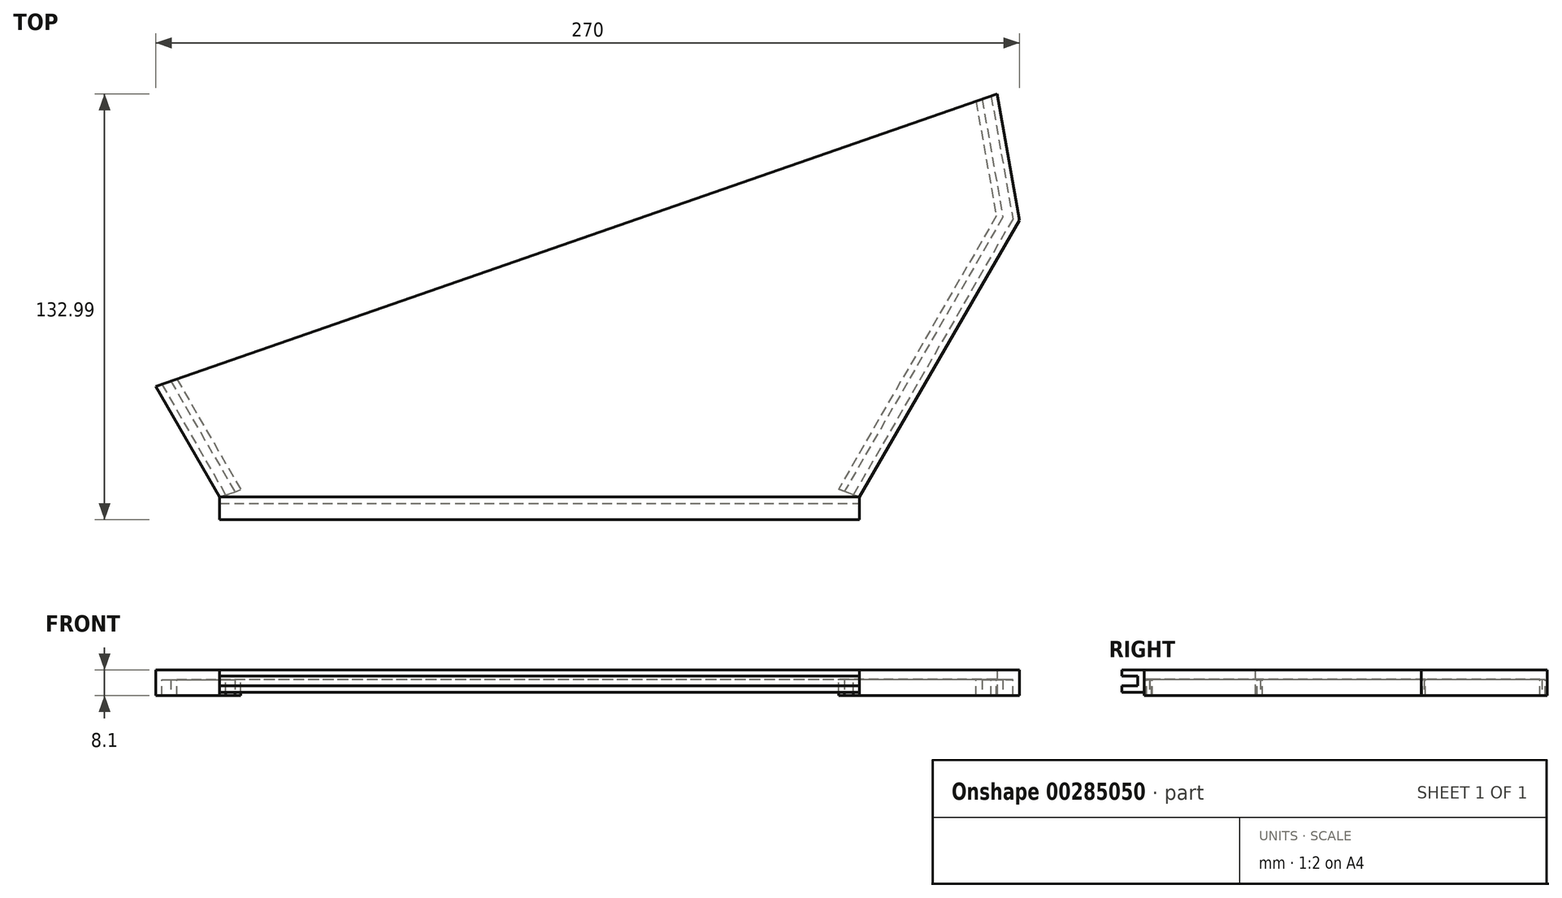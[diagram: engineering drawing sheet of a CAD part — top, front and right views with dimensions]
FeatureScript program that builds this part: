
annotation { "Feature Type Name" : "Feature", "Feature Type Description" : "" }
export const myFeature = defineFeature(function(context is Context, id is Id, definition is map)
    precondition{}
    {
        {
            var Q0;
            Q0=qCreatedBy(makeId("Top.planeOp"),FACE);
            var sketch = newSketch(context, id + "F0", { "sketchPlane" : qUnion([Q0])});
            skLineSegment(sketch, "E0", {"start": v(-20, 34.64) * mm, "end": v(0, 0) * mm});
            skLineSegment(sketch, "E1", {"start": v(0, 0) * mm, "end": v(200, 0) * mm});
            skLineSegment(sketch, "E2", {"start": v(200, 0) * mm, "end": v(250, 86.6) * mm});
            skLineSegment(sketch, "E3", {"start": v(250, 86.6) * mm, "end": v(243.05, 126) * mm});
            skLineSegment(sketch, "E4", {"start": v(-20, 34.64) * mm, "end": v(243.05, 126) * mm});
            skSolve(sketch);
        }
        {
            var Q0;
            Q0=makeQuery(id+"F0.imprint","IMPRINT",FACE,{"disambiguationData":[TD([[makeQuery(id+"F0.imprint","IMPRINT",EDGE,{"derivedFrom":sQuery(id+"F0.wireOp",EDGE,"E0")}),1.0]])]});
            extrude(context, id + "F1", {"entities" : qUnion([Q0]), "depth" : 3 * mm});
        }
        {
            var Q0;
            Q0=makeQuery(id+"F1.opExtrude","SWEPT_FACE",FACE,{"disambiguationData":[OSD([sQuery(id+"F0.wireOp",EDGE,"E4")])]});
            var sketch = newSketch(context, id + "F2", { "sketchPlane" : qUnion([Q0])});
            skLineSegment(sketch, "E5", {"start": v(7.53, 0) * mm, "end": v(7.53, -5.1) * mm});
            skLineSegment(sketch, "E6", {"start": v(7.53, -5.1) * mm, "end": v(5.53, -5.1) * mm});
            skLineSegment(sketch, "E7", {"start": v(5.53, -5.1) * mm, "end": v(5.53, -0.1) * mm});
            skLineSegment(sketch, "E8", {"start": v(5.53, -0.1) * mm, "end": v(2.53, -0.1) * mm});
            skLineSegment(sketch, "E9", {"start": v(2.53, -0.1) * mm, "end": v(2.53, -5.1) * mm});
            skLineSegment(sketch, "E10", {"start": v(2.53, -5.1) * mm, "end": v(0.53, -5.1) * mm});
            skLineSegment(sketch, "E11", {"start": v(0.53, -5.1) * mm, "end": v(0.53, 0) * mm});
            skSolve(sketch);
        }
        {
            var Q0;
            {var subQ0=sQuery(id+"F0.wireOp",EDGE,"E4");Q0=makeQuery(id+"F4.boolean.opBoolean","MERGE",FACE,{"derivedFrom":[makeQuery(id+"F1.opExtrude","SWEPT_FACE",FACE,{"disambiguationData":[OSD([subQ0])]}),makeQuery(id+"F4.opSweep","CAP_FACE",FACE,{"disambiguationData":[OSD([sQuery(id+"F0.wireOp",EDGE,"E0"),subQ0,sQuery(id+"F2.wireOp",EDGE,"E5"),sQuery(id+"F2.wireOp",EDGE,"E6"),sQuery(id+"F2.wireOp",EDGE,"E7"),sQuery(id+"F2.wireOp",EDGE,"E8"),sQuery(id+"F2.wireOp",EDGE,"E9"),sQuery(id+"F2.wireOp",EDGE,"E10"),sQuery(id+"F2.wireOp",EDGE,"E11")])],"isStart":true})]});}
            var sketch = newSketch(context, id + "F3", { "sketchPlane" : qUnion([Q0])});
            skLineSegment(sketch, "E12", {"start": v(-270.94, 0) * mm, "end": v(-270.94, -5.1) * mm});
            skLineSegment(sketch, "E13", {"start": v(-270.94, -5.1) * mm, "end": v(-268.94, -5.1) * mm});
            skLineSegment(sketch, "E14", {"start": v(-268.94, -5.1) * mm, "end": v(-268.94, -0.1) * mm});
            skLineSegment(sketch, "E15", {"start": v(-268.94, -0.1) * mm, "end": v(-265.94, -0.1) * mm});
            skLineSegment(sketch, "E16", {"start": v(-265.94, -0.1) * mm, "end": v(-265.94, -5.1) * mm});
            skLineSegment(sketch, "E17", {"start": v(-265.94, -5.1) * mm, "end": v(-263.94, -5.1) * mm});
            skLineSegment(sketch, "E18", {"start": v(-263.94, -5.1) * mm, "end": v(-263.94, 0) * mm});
            skLineSegment(sketch, "E19", {"start": v(-263.94, 0) * mm, "end": v(-270.94, 0) * mm});
            skSolve(sketch);
        }
        {
            var Q0;
            {var subQ0=sQuery(id+"F2.wireOp",EDGE,"E5");Q0=makeQuery(id+"F2.imprint","IMPRINT",FACE,{"disambiguationData":[TD([[makeQuery(id+"F2.imprint","IMPRINT",EDGE,{"derivedFrom":subQ0}),-1.0]])]});}
            var Q1;
            Q1=makeQuery(id+"F1.opExtrude","CAP_EDGE",EDGE,{"disambiguationData":[OSD([sQuery(id+"F0.wireOp",EDGE,"E0")])],"isStart":true});
            sweep(context, id + "F4", {"operationType" : NewBodyOperationType.ADD, "profiles" : qUnion([Q0]), "path" : qUnion([Q1])});
        }
        {
            var Q0;
            Q0=qCreatedBy(makeId("Right.planeOp"),FACE);
            var sketch = newSketch(context, id + "F5", { "sketchPlane" : qUnion([Q0])});
            skLineSegment(sketch, "E20.0", {"start": v(0, 3) * mm, "end": v(0, 0) * mm});
            skLineSegment(sketch, "E21.0", {"start": v(0, 0) * mm, "end": v(0, -5.1) * mm});
            skLineSegment(sketch, "E22", {"start": v(0, 3) * mm, "end": v(-7, 3) * mm});
            skLineSegment(sketch, "E23", {"start": v(-7, 3) * mm, "end": v(-7, 1) * mm});
            skLineSegment(sketch, "E24", {"start": v(-7, 1) * mm, "end": v(-2, 1) * mm});
            skLineSegment(sketch, "E25", {"start": v(-2, 1) * mm, "end": v(-2, -2) * mm});
            skLineSegment(sketch, "E26", {"start": v(-2, -2) * mm, "end": v(-7, -2) * mm});
            skLineSegment(sketch, "E27", {"start": v(-7, -2) * mm, "end": v(-7, -4) * mm});
            skLineSegment(sketch, "E28", {"start": v(-7, -4) * mm, "end": v(0, -4) * mm});
            skLineSegment(sketch, "E29", {"start": v(0, -4) * mm, "end": v(0, 0) * mm});
            skSolve(sketch);
        }
        {
            var Q0;
            Q0=makeQuery(id+"F3.imprint","IMPRINT",FACE,{"disambiguationData":[TD([[makeQuery(id+"F3.imprint","IMPRINT",EDGE,{"derivedFrom":sQuery(id+"F3.wireOp",EDGE,"E12")}),1.0]])]});
            var Q1;
            Q1=makeQuery(id+"F1.opExtrude","CAP_EDGE",EDGE,{"disambiguationData":[OSD([sQuery(id+"F0.wireOp",EDGE,"E3")])],"isStart":true});
            var Q2;
            Q2=makeQuery(id+"F1.opExtrude","CAP_EDGE",EDGE,{"disambiguationData":[OSD([sQuery(id+"F0.wireOp",EDGE,"E2")])],"isStart":true});
            sweep(context, id + "F6", {"operationType" : NewBodyOperationType.ADD, "profiles" : qUnion([Q0]), "path" : qUnion([Q1, Q2])});
        }
        {
            var Q0;
            Q0=makeQuery(id+"F5.imprint","IMPRINT",FACE,{"disambiguationData":[TD([[makeQuery(id+"F5.imprint","IMPRINT",EDGE,{"derivedFrom":sQuery(id+"F5.wireOp",EDGE,"E20.0")}),-1.0]])]});
            var Q1;
            Q1=makeQuery(id+"F1.opExtrude","CAP_EDGE",EDGE,{"disambiguationData":[OSD([sQuery(id+"F0.wireOp",EDGE,"E1")])],"isStart":false});
            sweep(context, id + "F7", {"profiles" : qUnion([Q0]), "path" : qUnion([Q1])});
        }
    });
